# Revit family: POL4_63_UN_Wall-fixture_ETK
name_source: partatom
category: Lighting Fixtures
revit_build: Autodesk Revit 2017 (Build: 20190508_0315(x64)
units: mm (PartAtom-declared; Revit-internal decimal feet)

## family parameters
Always vertical = Yes
Cut with Voids When Loaded = No
Light Source = No
OmniClass Number = 23.80.70.11.14
OmniClass Title = General Luminaries, Directional
Part Type = Normal
Room Calculation Point = Yes
Round Connector Dimension = Use Diameter
Shared = No
Work Plane-Based = No

## types (4) — shared parameters
Apparent Load = 13 VA
Assembly Code = 63.0
Description = Wall-fixture
IfcExportAs = IfcLightFixtureType
IfcExportType = USERDEFINED
Lamp = LED
Luminaire_Body_Material = 10 White
Manufacturer = ETK licht B.V.
Model = POL4
URL = https://www.etk.nl
Voltage = 230 V
Wattage Comments = 12.5W

## per-type parameters (varying)
| type | Light Source |
| POL.4100.xx - 12.5W / 1400lm / 3000K | POL.4 - Lightsource : POL.4100.xx - 12.5W / 1400lm / 3000K |
| POL.4200.xx - 12.5W / 1470lm / 4000K | POL.4 - Lightsource : POL.4200.xx - 12.5W / 1470lm / 4000K |
| POL.4300.xx - 17W / 2100lm / 3000K | POL.4 - Lightsource : POL.4300.xx - 17W / 2100lm / 3000K |
| POL.4400.xx - 17W / 2240lm / 4000K | POL.4 - Lightsource : POL.4400.xx - 17W / 2240lm / 4000K |

## geometry (parser evidence)
native form markers: Sweep x6
no freeform markers — native parametric forms only
